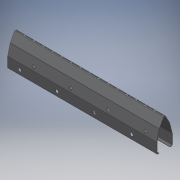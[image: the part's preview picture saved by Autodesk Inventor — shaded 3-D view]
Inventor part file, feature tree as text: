
AUTODESK INVENTOR PART (.ipt)
format: ipt  version: 2018 (Build 220112000, 112)  size: 840,704 bytes
history: native  units: mm
features: reference x25, other x24, sketch x14, sheet_metal_op x13, plane x9, projected_geometry x7, extrude x4
ambient origin geometry x8: Origin, YZ Plane, XZ Plane, XY Plane, X Axis, Y Axis, Z Axis, Center Point
bodies: Solid1 (feature_tree)
feature tree (96):
  parser-record x5  (decoder bookkeeping rows leaked as tree rows — omitted from the tree; the rows remain in map.json)
  plane  "Work Plane1"
  sheet_metal_op  "Face1"
  plane  "Work Plane2"
  sheet_metal_op  "Face2"
  plane  "Work Plane3"
  sheet_metal_op  "Face3"
  plane  "Work Plane4"
  sheet_metal_op  "Face4"
  plane  "Work Plane5"
  sheet_metal_op  "Face5"
  plane  "Work Plane6"
  sheet_metal_op  "Face6"
  plane  "Work Plane7"
  sheet_metal_op  "Face7"
  other  "midtplan"
  extrude  "Extrusion3"  Depth=5.0mm
  extrude  "hulsæt til stifter"  Depth=2.0mm
  plane  "Work Plane11"
  sketch  "Sketch13"  dims[d13=2.0mm]
  plane  "Work Plane12"
  extrude  "balusterhul"  Depth=5.0mm
  extrude  "balusterhul skråkompensering"  Depth=4.0mm
  sketch  "Sketch1"  dims[d0=4.0mm d1=5.0mm]
  reference  "Reference1"
  reference  "Reference2"
  reference  "Reference3"
  reference  "Reference4"
  other  "Plate1"
  sketch  "Sketch2"  dims[d2=4.0mm d3=2.0mm]
  reference  "Reference5"
  reference  "Reference6"
  reference  "Reference7"
  reference  "Reference8"
  other  "Plate2"
  sheet_metal_op  "Bend1"
  sketch  "Sketch3"  dims[d4=8.0mm d5=5.0mm]
  reference  "Reference9"
  reference  "Reference10"
  reference  "Reference11"
  other  "Plate3"
  sheet_metal_op  "Bend2"
  sketch  "Sketch4"  dims[d6=5.0mm d7=4.0mm]
  reference  "Reference12"
  reference  "Reference13"
  reference  "Reference14"
  reference  "Reference15"
  other  "Plate4"
  sheet_metal_op  "Bend3"
  sketch  "Sketch5"  dims[d8=2.0mm]
  reference  "Reference16"
  reference  "Reference17"
  reference  "Reference18"
  other  "Plate5"
  sheet_metal_op  "Bend4"
  sketch  "Sketch6"  dims[d9=8.0mm]
  reference  "Reference19"
  reference  "Reference20"
  reference  "Reference21"
  other  "Plate6"
  sheet_metal_op  "Bend5"
  sketch  "Sketch7"  dims[d10=5.0mm]
  reference  "Reference22"
  reference  "Reference23"
  other  "Plate7"
  sheet_metal_op  "Bend6"
  sketch  "Sketch8"  dims[d11=5.0mm]
  reference  "Reference24"
  projected_geometry  "Projected Loop1"
  other  "huller til stifter"
  projected_geometry  "Projected Loop3"
  sketch  "Sketch12"  dims[d12=4.0mm]
  projected_geometry  "Projected Loop4"
  reference  "Reference25"
  sketch  "Sketch14"  dims[d14=8.0mm]
  sketch  "Sketch15"  dims[d15=5.0mm]
  projected_geometry  "Projected Loop5"
  projected_geometry  "Projected Loop6"
  sketch  "Sketch16"  dims[d16=5.0mm]
  projected_geometry  "Projected Loop7"
  projected_geometry  "Projected Loop8"
  sketch  "Sketch17"  dims[d17=4.0mm d18=2.0mm d19=8.0mm d20=5.0mm d21=5.0mm d22=4.0mm d23=2.0mm d24=8.0mm d25=5.0mm d26=5.0mm d27=4.0mm d28=2.0mm d29=8.0mm d30=5.0mm d31=4.0mm d32=0.0mm d33=3.0mm d39=250.0mm d41=33.7mm d42=33.7mm d43=60.0mm d44=60.0mm d45=16.85mm d46=65.0mm d47=60.0mm d48=10.0mm d49=0.0mm d68=291.052mm d69=10.0mm d70=0.0mm d73=96.672mm d77=40.001254mm d78=26.6mm d79=25.8mm d80=40.0mm d82=302.737mm d83=10.0mm d85=10.0mm d87=302.737mm d88=113.655385mm d89=56.827692mm d90=90.0deg d91=90.0deg d92=49.5mm d93=100.0mm d94=0.0mm d97=2.728615mm d98=1.364307mm d99=10.0mm d100=0.0mm d101=90.0mm d102=30.0mm d103=521.995413mm d104=342.76471mm d106=342.76471mm d107=30.0mm d108=30.0mm d109=342.76471mm d110=30.0mm d111=342.76471mm d112=624.298717mm d113=10.0mm d114=4.0mm d115=0.0mm d116=221.534007mm d117=119.230703mm d118=96.672222mm d119=62.65387mm d120=1208.948mm d121=8.0mm d122=62.8mm d123=6.0mm d124=170.0mm d126=75.36mm d127=10.0mm d129=10.0mm d131=4.0mm d132=0.0mm d133=12.56mm]
  other  "Cut1"
  other  "plantehuller"
  other  "bukkeperforering"
  other  "modul.iam"
  other  "model:1"
  other  "Definition1"
  other  "søjle+vange.iam"
  other  "modul top:1"
  other  "plade top:1"
  other  "modul top.iam"
note: 5 file-system paths scrubbed to <path> (originals preserved in map.json)
